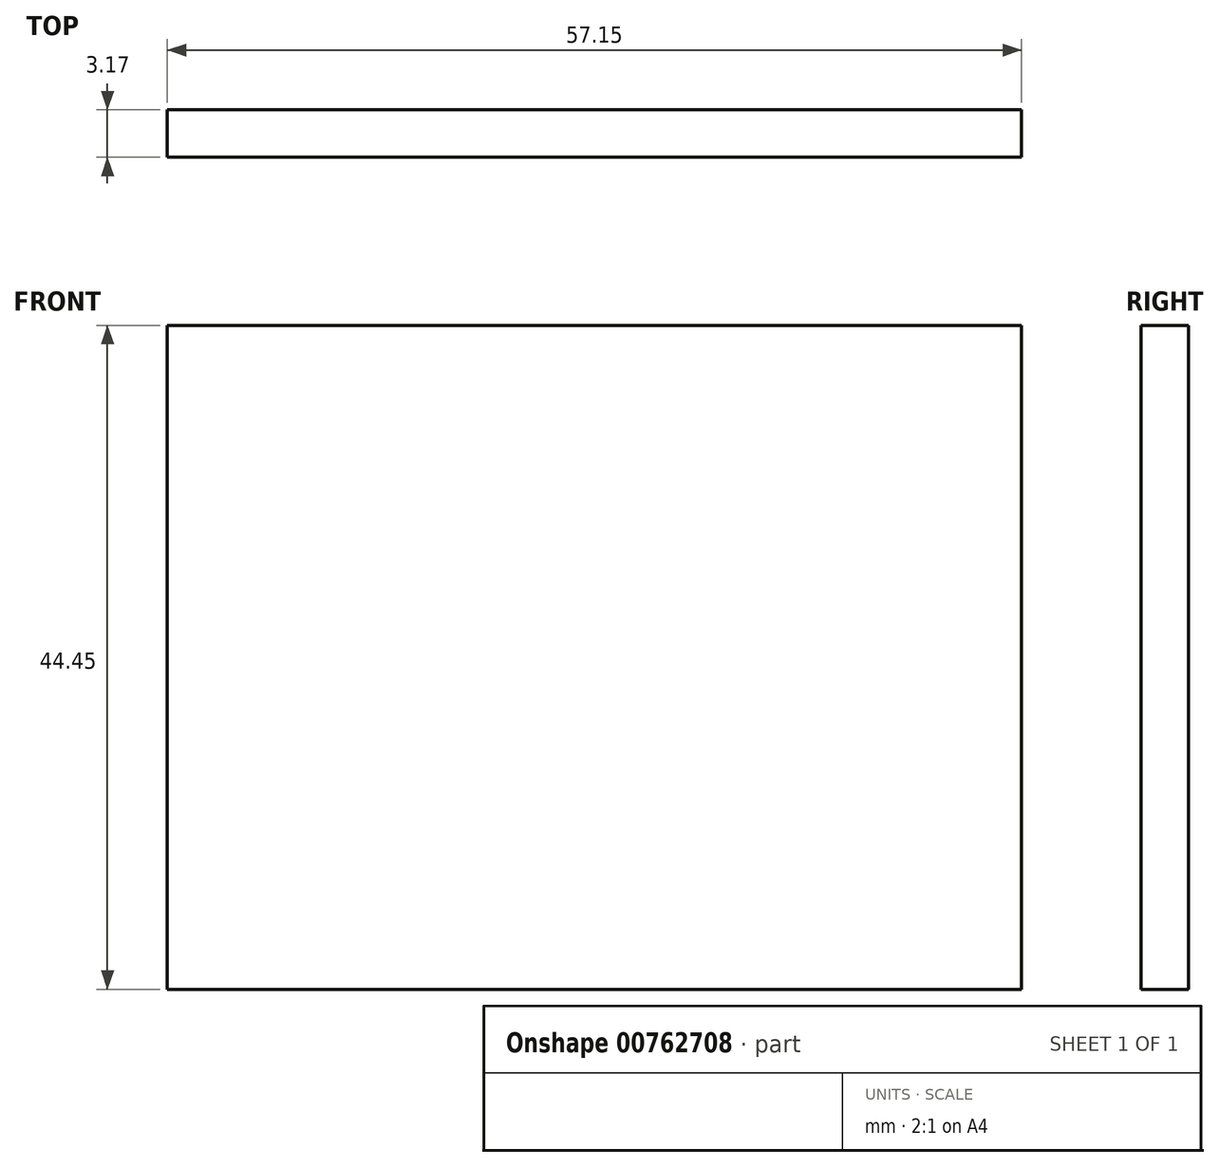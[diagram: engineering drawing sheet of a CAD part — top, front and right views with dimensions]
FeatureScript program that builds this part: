
annotation { "Feature Type Name" : "Feature", "Feature Type Description" : "" }
export const myFeature = defineFeature(function(context is Context, id is Id, definition is map)
    precondition{}
    {
        {
            var Q0;
            Q0=qCreatedBy(makeId("Front.planeOp"),FACE);
            var sketch = newSketch(context, id + "F0", { "sketchPlane" : qUnion([Q0])});
            skLineSegment(sketch, "E0.bottom", {"start": v(0, 0) * mm, "end": v(57.15, 0) * mm});
            skLineSegment(sketch, "E0.top", {"start": v(0, 44.45) * mm, "end": v(57.15, 44.45) * mm});
            skLineSegment(sketch, "E0.left", {"start": v(0, 0) * mm, "end": v(0, 44.45) * mm});
            skLineSegment(sketch, "E0.right", {"start": v(57.15, 0) * mm, "end": v(57.15, 44.45) * mm});
            skSolve(sketch);
        }
        {
            var Q0;
            Q0 = qSketchRegion(id + "F0", true);
            extrude(context, id + "F1", {"entities" : qUnion([Q0]), "oppositeDirection" : true, "depth" : 3.17 * mm, "offsetDistance" : 25.4 * mm});
        }
    });
